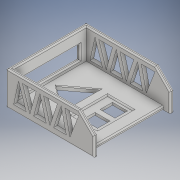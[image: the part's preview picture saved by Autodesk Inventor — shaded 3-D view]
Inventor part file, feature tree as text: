
AUTODESK INVENTOR PART (.ipt)
format: ipt  version: 2018 (Build 220112000, 112)  size: 312,320 bytes
history: native  units: in
note: dims shown in document units (in); Inventor stores cm internally (conversion verified against a paired STEP export)
features: extrude x8, sketch x8, fillet x2, chamfer x1
ambient origin geometry x8: Origin, YZ Plane, XZ Plane, XY Plane, X Axis, Y Axis, Z Axis, Center Point
bodies: Solid1 (feature_tree)
feature tree (19):
  extrude  "Extrusion1"  Depth=6.2992in
  extrude  "Extrusion2"  TaperAngle=0.0deg  [1 undecoded]
  extrude  "Extrusion3"  Depth=0.2953in
  extrude  "Extrusion4"  Depth=6.5945in
  chamfer  "Chamfer1"  Distance=2.3622in
  extrude  "Extrusion5"  Depth=0.7874in
  extrude  "Extrusion6"  Depth=0.9843in
  fillet  "Fillet1"  Radius=4.7244in
  extrude  "Extrusion7"  Depth=2.3622in TaperAngle=0.0deg
  extrude  "Extrusion8"  Depth=0.2953in TaperAngle=0.0deg
  fillet  "Fillet2"  Radius=0.4921in
  sketch  "Sketch1"  dims[d0=6.8898in d1=6.2992in]
  sketch  "Sketch2"  dims[d2=0.2953in d3=0.0in]
  sketch  "Sketch3"  dims[d4=0.2953in d5=0.2953in]
  sketch  "Sketch4"  dims[d6=5.7087in d7=6.5945in]
  sketch  "Sketch5"  dims[d8=0.4921in d9=2.3622in d10=0.0in]
  sketch  "Sketch6"  dims[d11=0.7874in d12=0.7874in]
  sketch  "Sketch9"  dims[d13=0.2953in d14=0.9843in d15=4.7244in]
  sketch  "Sketch10"  dims[d16=1.0827in d17=2.3622in d18=0.0in d19=0.2953in d20=0.0in d21=0.4921in d22=0.2953in d23=0.0in d24=1.1811in d25=0.0492in d26=45.0deg d27=1.1811in d28=1.1811in d29=0.3937in d30=1.9685in d31=1.9685in d32=0.9843in d33=1.1811in d34=1.1811in d35=0.2953in d36=0.0in d37=0.1969in d38=0.5906in d39=0.1969in d40=0.1969in d41=0.0984in d42=0.0in d45=0.0984in d48=0.2953in d49=0.3937in d50=0.2953in d51=0.2953in d52=0.2953in d53=0.2953in d54=0.2953in d55=0.2953in d56=1.0827in d57=1.0827in d58=1.0827in d59=0.9843in d60=0.9843in d61=0.9843in d62=0.3937in d63=0.0in d64=0.2953in d65=0.689in d66=2.9528in d67=1.378in d68=1.378in d69=0.5906in d70=1.9685in d71=1.4764in d72=0.3937in d73=0.0in d74=0.0591in]
note: 1 required parameter value undecoded (feature->parameter linkage not recoverable at this tier; creation-order binding heuristic only, values carry confidence <= 0.55)
